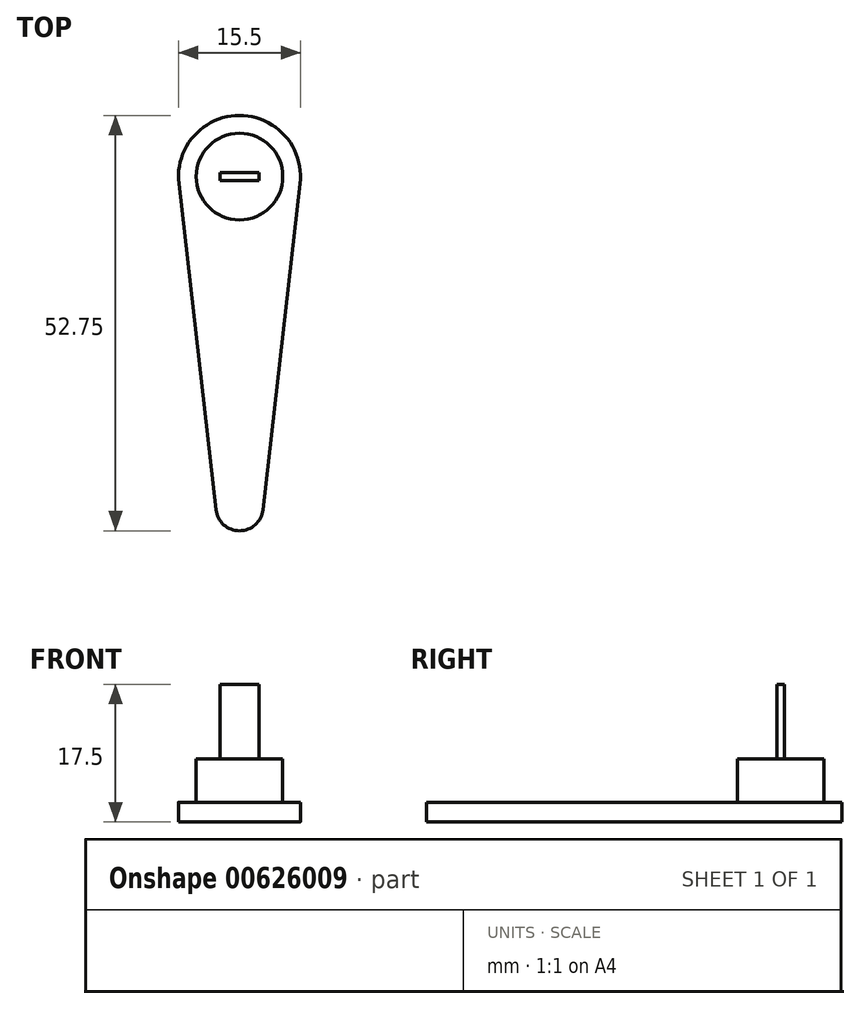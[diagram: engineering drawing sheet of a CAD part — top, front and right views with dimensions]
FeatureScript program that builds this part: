
annotation { "Feature Type Name" : "Feature", "Feature Type Description" : "" }
export const myFeature = defineFeature(function(context is Context, id is Id, definition is map)
    precondition{}
    {
        {
            var Q0;
            Q0=qCreatedBy(makeId("Top.planeOp"),FACE);
            var sketch = newSketch(context, id + "F0", { "sketchPlane" : qUnion([Q0])});
            skLineSegment(sketch, "E0.bottom", {"start": v(-2.5, -0.5) * mm, "end": v(2.5, -0.5) * mm});
            skLineSegment(sketch, "E0.top", {"start": v(-2.5, 0.5) * mm, "end": v(2.5, 0.5) * mm});
            skLineSegment(sketch, "E0.left", {"start": v(-2.5, 0.5) * mm, "end": v(-2.5, -0.5) * mm});
            skLineSegment(sketch, "E0.right", {"start": v(2.5, 0.5) * mm, "end": v(2.5, -0.5) * mm});
            skCircle(sketch, "E1", {"center": v(0, 0) * mm, "radius": 5.5 * mm});
            skCircle(sketch, "E2", {"center": v(0, 0) * mm, "radius": 7.75 * mm});
            skCircle(sketch, "E3", {"center": v(0, -42) * mm, "radius": 3 * mm});
            skLineSegment(sketch, "E4", {"start": v(-7.7, -0.88) * mm, "end": v(-2.98, -42.34) * mm});
            skLineSegment(sketch, "E5", {"start": v(7.7, -0.88) * mm, "end": v(2.98, -42.34) * mm});
            skSolve(sketch);
        }
        {
            var Q0;
            Q0=makeQuery(id+"F0.imprint","IMPRINT",FACE,{"disambiguationData":[TD([[makeQuery(id+"F0.imprint","IMPRINT",EDGE,{"derivedFrom":sQuery(id+"F0.wireOp",EDGE,"E0.bottom")}),1.0]])]});
            extrude(context, id + "F1", {"entities" : qUnion([Q0]), "depth" : 15 * mm, "offsetDistance" : 25 * mm});
        }
        {
            var Q0;
            Q0=makeQuery(id+"F0.imprint","IMPRINT",FACE,{"disambiguationData":[TD([[makeQuery(id+"F0.imprint","IMPRINT",EDGE,{"derivedFrom":sQuery(id+"F0.wireOp",EDGE,"E0.bottom")}),-1.0]])]});
            extrude(context, id + "F2", {"entities" : qUnion([Q0]), "operationType" : NewBodyOperationType.ADD, "depth" : 5.5 * mm, "offsetDistance" : 25 * mm});
        }
        {
            var Q0;
            {var subQ0=sQuery(id+"F0.wireOp",EDGE,"E4");Q0=makeQuery(id+"F0.imprint","IMPRINT",FACE,{"disambiguationData":[TD([[makeQuery(id+"F0.imprint","IMPRINT",EDGE,{"derivedFrom":subQ0}),1.0]])]});}
            var Q1;
            {var subQ0=sQuery(id+"F0.wireOp",EDGE,"E3");var subQ1=makeQuery(id+"F0.imprint","INTERSECT",VERTEX,{"derivedFrom":[subQ0,sQuery(id+"F0.wireOp",EDGE,"E4")]});Q1=makeQuery(id+"F0.imprint","IMPRINT",FACE,{"disambiguationData":[TD([[makeQuery(id+"F0.imprint","IMPRINT",EDGE,{"disambiguationData":[TD([[subQ1,-1.0]])],"derivedFrom":subQ0}),1.0]])]});}
            var Q2;
            Q2=makeQuery(id+"F0.imprint","IMPRINT",FACE,{"disambiguationData":[TD([[makeQuery(id+"F0.imprint","IMPRINT",EDGE,{"derivedFrom":sQuery(id+"F0.wireOp",EDGE,"E0.bottom")}),1.0]])]});
            var Q3;
            Q3=makeQuery(id+"F0.imprint","IMPRINT",FACE,{"disambiguationData":[TD([[makeQuery(id+"F0.imprint","IMPRINT",EDGE,{"derivedFrom":sQuery(id+"F0.wireOp",EDGE,"E0.bottom")}),-1.0]])]});
            var Q4;
            Q4=makeQuery(id+"F0.imprint","IMPRINT",FACE,{"disambiguationData":[TD([[makeQuery(id+"F0.imprint","IMPRINT",EDGE,{"derivedFrom":sQuery(id+"F0.wireOp",EDGE,"E1")}),-1.0]])]});
            extrude(context, id + "F3", {"entities" : qUnion([Q0, Q1, Q2, Q3, Q4]), "operationType" : NewBodyOperationType.ADD, "oppositeDirection" : true, "depth" : 2.5 * mm, "offsetDistance" : 25 * mm});
        }
    });
